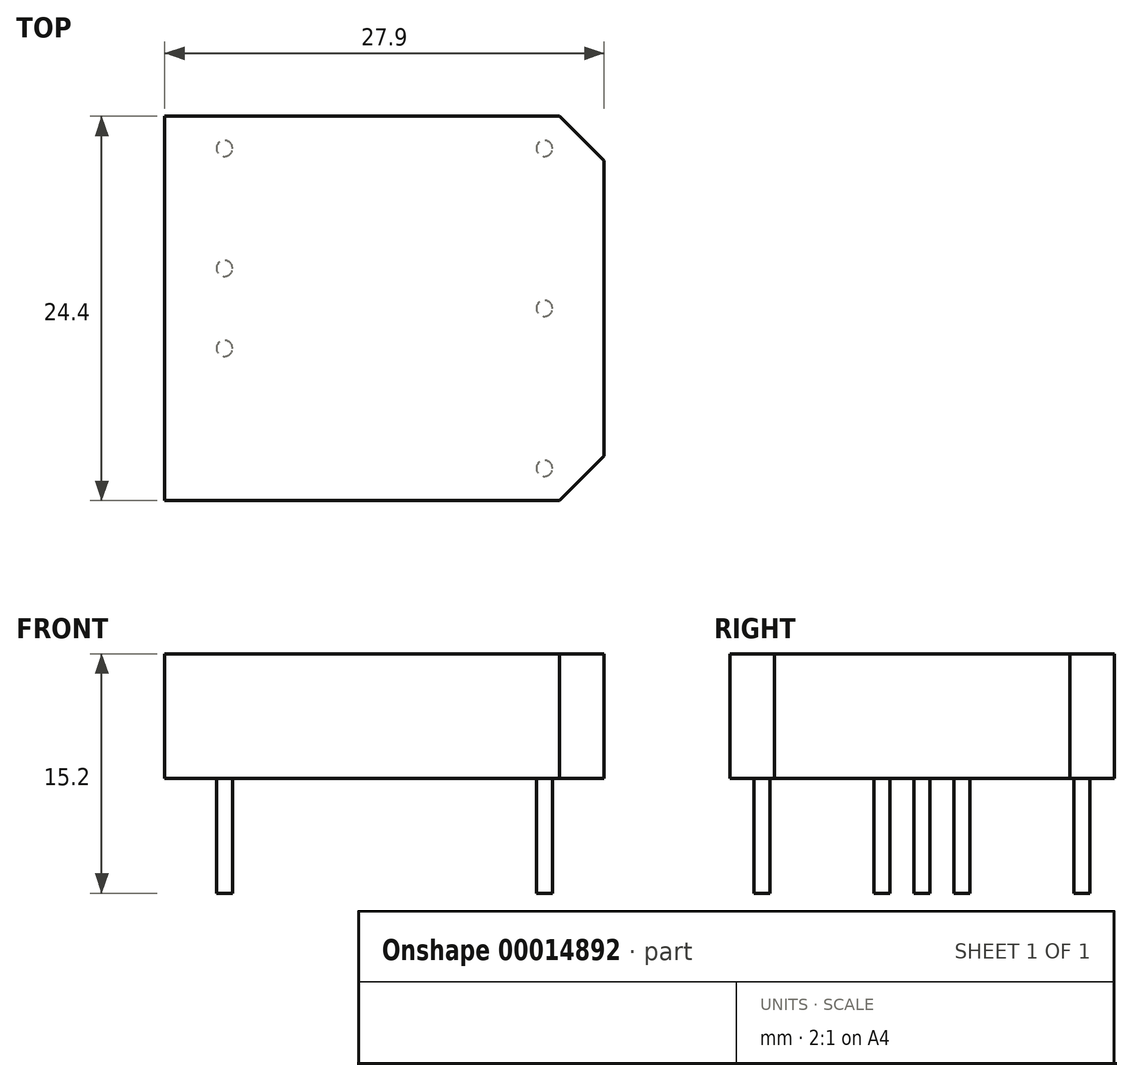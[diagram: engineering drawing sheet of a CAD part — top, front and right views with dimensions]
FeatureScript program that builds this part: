
annotation { "Feature Type Name" : "Feature", "Feature Type Description" : "" }
export const myFeature = defineFeature(function(context is Context, id is Id, definition is map)
    precondition{}
    {
        {
            var Q0;
            Q0=qCreatedBy(makeId("Top.planeOp"),FACE);
            var sketch = newSketch(context, id + "F0", { "sketchPlane" : qUnion([Q0])});
            skLineSegment(sketch, "E0.left", {"start": v(-13.95, 12.2) * mm, "end": v(-13.95, -12.2) * mm});
            skLineSegment(sketch, "E1", {"start": v(11.12, 12.2) * mm, "end": v(13.95, 9.37) * mm});
            skLineSegment(sketch, "E2", {"start": v(13.95, -9.37) * mm, "end": v(11.12, -12.2) * mm});
            skLineSegment(sketch, "E3", {"start": v(-13.95, 12.2) * mm, "end": v(11.12, 12.2) * mm});
            skLineSegment(sketch, "E4", {"start": v(13.95, 9.37) * mm, "end": v(13.95, -9.37) * mm});
            skLineSegment(sketch, "E5", {"start": v(11.12, -12.2) * mm, "end": v(-13.95, -12.2) * mm});
            skSolve(sketch);
        }
        {
            var Q0;
            Q0=makeQuery(id+"F0.imprint","IMPRINT",FACE,{"disambiguationData":[TD([[makeQuery(id+"F0.imprint","IMPRINT",EDGE,{"derivedFrom":sQuery(id+"F0.wireOp",EDGE,"E0.left")}),1.0]])]});
            extrude(context, id + "F1", {"entities" : qUnion([Q0]), "depth" : 7.9 * mm});
        }
        {
            var Q0;
            Q0=makeQuery(id+"F1.opExtrude","CAP_FACE",FACE,{"disambiguationData":[OSD([sQuery(id+"F0.wireOp",EDGE,"E0.left"),sQuery(id+"F0.wireOp",EDGE,"E1"),sQuery(id+"F0.wireOp",EDGE,"E2"),sQuery(id+"F0.wireOp",EDGE,"E3"),sQuery(id+"F0.wireOp",EDGE,"E4"),sQuery(id+"F0.wireOp",EDGE,"E5")])],"isStart":true});
            var sketch = newSketch(context, id + "F2", { "sketchPlane" : qUnion([Q0])});
            skCircle(sketch, "E6", {"center": v(-10.16, 2.54) * mm, "radius": 0.5 * mm});
            skCircle(sketch, "E7", {"center": v(-10.16, -2.54) * mm, "radius": 0.5 * mm});
            skCircle(sketch, "E8", {"center": v(-10.16, -10.16) * mm, "radius": 0.5 * mm});
            skCircle(sketch, "E9", {"center": v(10.16, 10.16) * mm, "radius": 0.5 * mm});
            skCircle(sketch, "E10", {"center": v(10.16, 0) * mm, "radius": 0.5 * mm});
            skCircle(sketch, "E11", {"center": v(10.16, -10.16) * mm, "radius": 0.5 * mm});
            skSolve(sketch);
        }
        {
            var Q0;
            Q0 = qSketchRegion(id + "F2", true);
            extrude(context, id + "F3", {"entities" : qUnion([Q0]), "depth" : 7.3 * mm});
        }
    });
